AUTODESK INVENTOR PART (.ipt)
format: ipt  version: 2014 SP2 (Build 180246200, 246)  size: 455,680 bytes
history: native  units: in
note: dims shown in document units (in); Inventor stores cm internally (conversion verified against a paired STEP export)
features: extrude x1, other x1, imported_body x1
ambient origin geometry x8: Origin, YZ Plane, XZ Plane, XY Plane, X Axis, Y Axis, Z Axis, Center Point
bodies: Body1 (feature_tree)
feature tree (3):
  extrude  "Extrude3"  [1 undecoded]
  other  "Fan_8312_NL_ebm-papst_8312 NL.ipt1"
  imported_body  "Base1"
note: 1 required parameter value undecoded (feature->parameter linkage not recoverable at this tier; creation-order binding heuristic only, values carry confidence <= 0.55)
